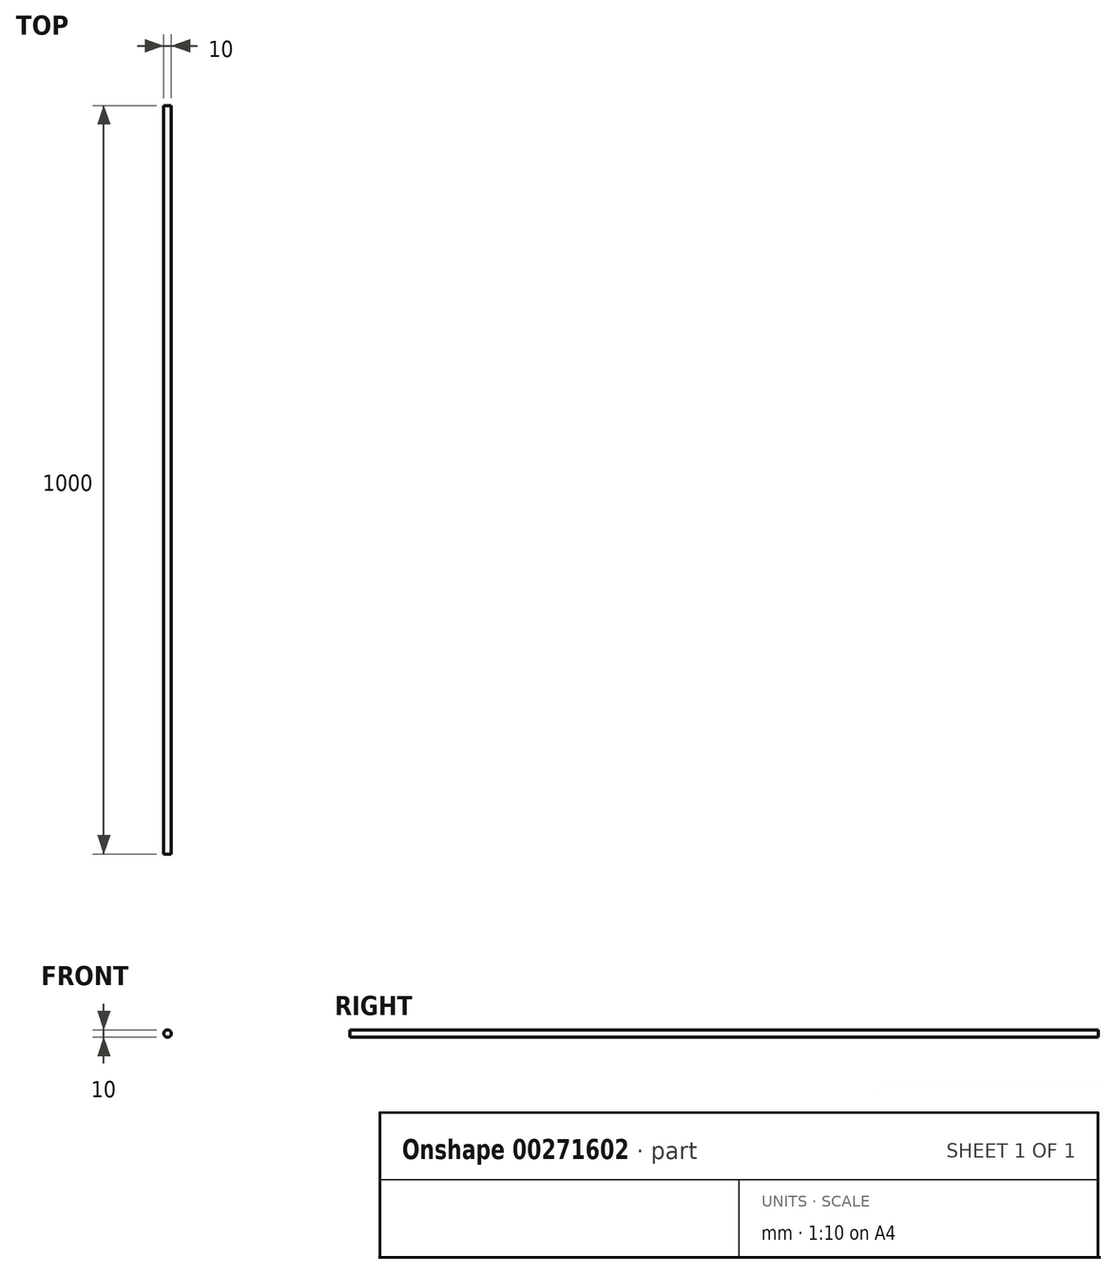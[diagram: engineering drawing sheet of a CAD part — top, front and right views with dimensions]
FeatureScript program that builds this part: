
annotation { "Feature Type Name" : "Feature", "Feature Type Description" : "" }
export const myFeature = defineFeature(function(context is Context, id is Id, definition is map)
    precondition{}
    {
        {
            var Q0;
            Q0=qCreatedBy(makeId("Front.planeOp"),FACE);
            var sketch = newSketch(context, id + "F0", { "sketchPlane" : qUnion([Q0])});
            skCircle(sketch, "E0", {"center": v(0, 0) * mm, "radius": 5 * mm});
            skSolve(sketch);
        }
        {
            var Q0;
            Q0=makeQuery(id+"F0.imprint","IMPRINT",FACE,{"disambiguationData":[TD([[makeQuery(id+"F0.imprint","IMPRINT",EDGE,{"derivedFrom":sQuery(id+"F0.wireOp",EDGE,"E0")}),1.0]])]});
            extrude(context, id + "F1", {"entities" : qUnion([Q0]), "oppositeDirection" : true, "depth" : 1000 * mm});
        }
    });
